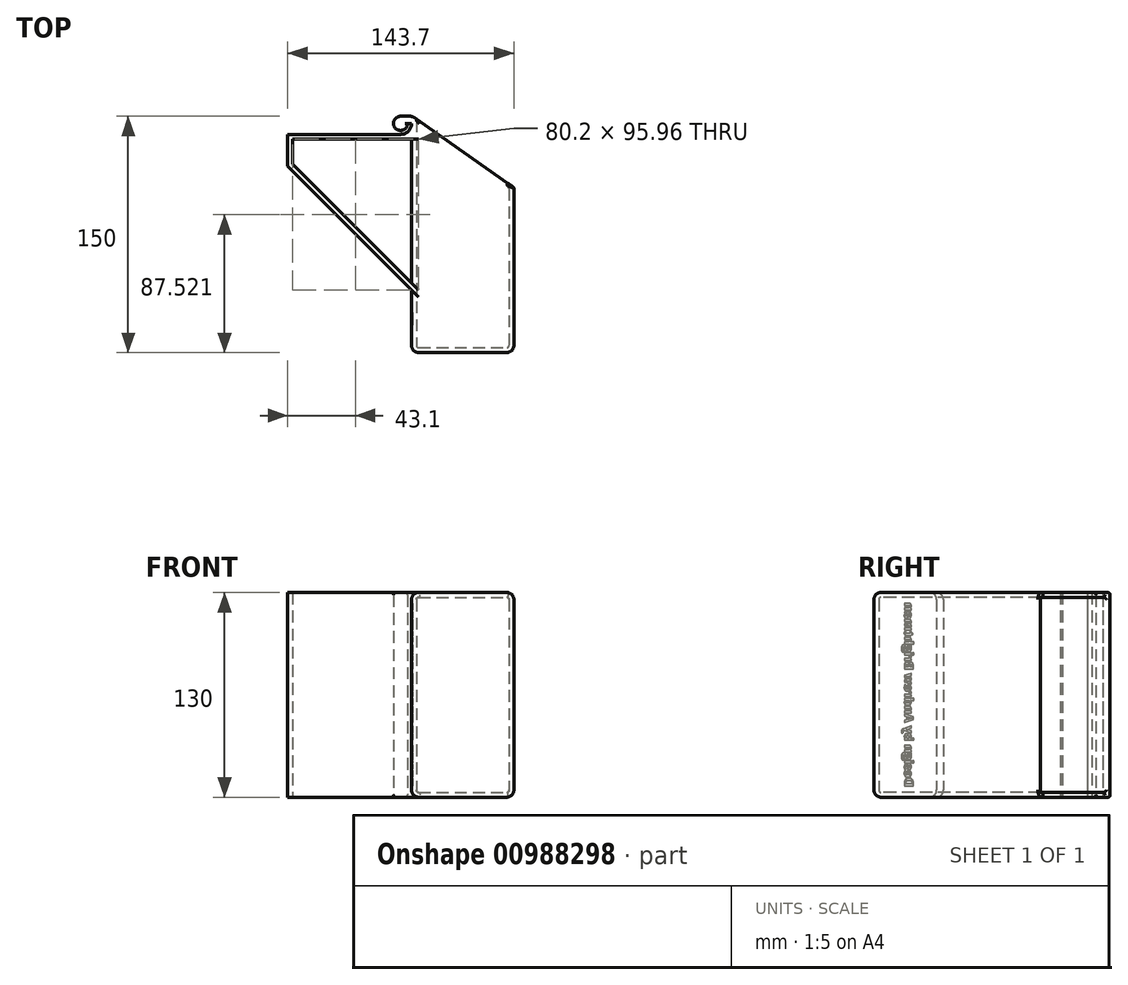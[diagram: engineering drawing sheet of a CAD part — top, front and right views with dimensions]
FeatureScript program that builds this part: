
annotation { "Feature Type Name" : "Feature", "Feature Type Description" : "" }
export const myFeature = defineFeature(function(context is Context, id is Id, definition is map)
    precondition{}
    {
        {
            assignVariable(context, id + "F0", {"variableType" : VariableType.LENGTH, "name" : "wallThickness", "lengthValue" : 3 * mm});
        }
        {
            var Q0;
            Q0=qCreatedBy(makeId("Top.planeOp"),FACE);
            var sketch = newSketch(context, id + "F1", { "sketchPlane" : qUnion([Q0])});
            skLineSegment(sketch, "E0", {"start": v(0, 0) * mm, "end": v(71.7, 0) * mm, "construction": true});
            skLineSegment(sketch, "E1", {"start": v(78.7, 7) * mm, "end": v(78.7, 7) * mm});
            skPoint(sketch, "E2.visualSharp", {"position": v(78.7, 0) * mm});
            skArc(sketch, "E2.filletArc", {"start": v(71.7, 0) * mm, "mid": v(76.65, 2.05) * mm, "end": v(78.7, 7) * mm, "construction": true});
            skArc(sketch, "E3.0", {"start": v(71.7, 2.5) * mm, "mid": v(74.88, 3.82) * mm, "end": v(76.2, 7) * mm, "construction": true});
            skLineSegment(sketch, "E3.1", {"start": v(0, 2.5) * mm, "end": v(71.7, 2.5) * mm, "construction": true});
            skLineSegment(sketch, "E4", {"start": v(0, 2.5) * mm, "end": v(0, 0) * mm, "construction": true});
            skLineSegment(sketch, "E5", {"start": v(76.2, 7) * mm, "end": v(78.7, 7) * mm, "construction": true});
            skLineSegment(sketch, "E6", {"start": v(0, 0) * mm, "end": v(0, -20) * mm});
            skLineSegment(sketch, "E7", {"start": v(0, -20) * mm, "end": v(0, -20) * mm});
            skLineSegment(sketch, "E8", {"start": v(78.7, -138.5) * mm, "end": v(143.7, -138.5) * mm});
            skLineSegment(sketch, "E9", {"start": v(143.7, -138.5) * mm, "end": v(143.7, -33.63) * mm});
            skLineSegment(sketch, "E10", {"start": v(143.7, -33.63) * mm, "end": v(80.54, 10.6) * mm});
            skArc(sketch, "E11.0", {"start": v(71.7, 0) * mm, "mid": v(76.65, 2.05) * mm, "end": v(78.7, 7) * mm});
            skLineSegment(sketch, "E11.1", {"start": v(0, 0) * mm, "end": v(71.7, 0) * mm});
            skArc(sketch, "E12", {"start": v(71.7, 11.5) * mm, "mid": v(68.52, 3.82) * mm, "end": v(76.2, 7) * mm});
            skLineSegment(sketch, "E13", {"start": v(77.67, 11.5) * mm, "end": v(71.7, 11.5) * mm});
            skLineSegment(sketch, "E14", {"start": v(76.2, 7) * mm, "end": v(78.7, 7) * mm});
            skLineSegment(sketch, "E15", {"start": v(78.7, 7) * mm, "end": v(81, 10.28) * mm, "construction": true});
            skPoint(sketch, "E16.visualSharp", {"position": v(79.25, 11.5) * mm});
            skArc(sketch, "E16.filletArc", {"start": v(80.54, 10.6) * mm, "mid": v(79.17, 11.27) * mm, "end": v(77.67, 11.5) * mm});
            skLineSegment(sketch, "E17", {"start": v(0, -20) * mm, "end": v(78.7, -98.7) * mm});
            skLineSegment(sketch, "E18.trimOffspring", {"start": v(78.7, -98.7) * mm, "end": v(78.7, -138.5) * mm});
            skLineSegment(sketch, "E19.0", {"start": v(3, -18.76) * mm, "end": v(78.7, -94.46) * mm});
            skLineSegment(sketch, "E20", {"start": v(78.7, -94.46) * mm, "end": v(78.7, -3) * mm});
            skLineSegment(sketch, "E21", {"start": v(78.7, -3) * mm, "end": v(3, -3) * mm});
            skLineSegment(sketch, "E22", {"start": v(3, -18.76) * mm, "end": v(3, -3) * mm});
            skSolve(sketch);
        }
        {
            var Q0;
            Q0 = qSketchRegion(id + "F1", true);
            extrude(context, id + "F2", {"entities" : qUnion([Q0]), "depth" : 130 * mm, "offsetDistance" : 25 * mm});
        }
        {
            var Q0;
            Q0=makeQuery(id+"F2.opExtrude","SWEPT_FACE",FACE,{"disambiguationData":[OSD([sQuery(id+"F1.wireOp",EDGE,"E8")])]});
            cPlane(context, id + "F3", {"entities" : qUnion([Q0]), "cplaneType" : CPlaneType.OFFSET, "offset" : getVariable(context, 'wallThickness'), "oppositeDirection" : true, "width" : 150 * mm, "height" : 150 * mm});
        }
        {
            var Q0;
            Q0=qCreatedBy(id+"F3.planeOp",FACE);
            var sketch = newSketch(context, id + "F4", { "sketchPlane" : qUnion([Q0])});
            skLineSegment(sketch, "E23.0", {"start": v(81.7, 127) * mm, "end": v(81.7, 3) * mm});
            skLineSegment(sketch, "E23.1", {"start": v(81.7, 127) * mm, "end": v(140.7, 127) * mm});
            skLineSegment(sketch, "E23.2", {"start": v(140.7, 127) * mm, "end": v(140.7, 3) * mm});
            skLineSegment(sketch, "E23.3", {"start": v(81.7, 3) * mm, "end": v(140.7, 3) * mm});
            skSolve(sketch);
        }
        {
            var Q0;
            Q0 = qSketchRegion(id + "F4", true);
            extrude(context, id + "F5", {"entities" : qUnion([Q0]), "operationType" : NewBodyOperationType.REMOVE, "endBound" : BoundingType.THROUGH_ALL, "oppositeDirection" : true, "depth" : 25 * mm, "offsetDistance" : 25 * mm});
        }
        {
            var Q0;
            Q0=makeQuery(id+"F5.boolean.opBoolean","COPY",FACE,{"derivedFrom":makeQuery(id+"F5.opExtrude","CAP_FACE",FACE,{"disambiguationData":[OSD([sQuery(id+"F4.wireOp",EDGE,"E23.0"),sQuery(id+"F4.wireOp",EDGE,"E23.1"),sQuery(id+"F4.wireOp",EDGE,"E23.2"),sQuery(id+"F4.wireOp",EDGE,"E23.3")])],"isStart":true})});
            var Q1;
            Q1=makeQuery(id+"F5.boolean.opBoolean","COPY",EDGE,{"derivedFrom":makeQuery(id+"F5.opExtrude","SWEPT_EDGE",EDGE,{"disambiguationData":[OSD([sQuery(id+"F4.wireOp",EDGE,"E23.0"),sQuery(id+"F4.wireOp",EDGE,"E23.3")])]})});
            var Q2;
            Q2=makeQuery(id+"F5.boolean.opBoolean","COPY",EDGE,{"derivedFrom":makeQuery(id+"F5.opExtrude","SWEPT_EDGE",EDGE,{"disambiguationData":[OSD([sQuery(id+"F4.wireOp",EDGE,"E23.2"),sQuery(id+"F4.wireOp",EDGE,"E23.3")])]})});
            var Q3;
            Q3=makeQuery(id+"F5.boolean.opBoolean","COPY",EDGE,{"derivedFrom":makeQuery(id+"F5.opExtrude","SWEPT_EDGE",EDGE,{"disambiguationData":[OSD([sQuery(id+"F4.wireOp",EDGE,"E23.0"),sQuery(id+"F4.wireOp",EDGE,"E23.1")])]})});
            var Q4;
            Q4=makeQuery(id+"F5.boolean.opBoolean","COPY",EDGE,{"derivedFrom":makeQuery(id+"F5.opExtrude","SWEPT_EDGE",EDGE,{"disambiguationData":[OSD([sQuery(id+"F4.wireOp",EDGE,"E23.1"),sQuery(id+"F4.wireOp",EDGE,"E23.2")])]})});
            fillet(context, id + "F6", {"entities" : qUnion([Q0, Q1, Q2, Q3, Q4]), "radius" : getVariable(context, 'wallThickness') / 2, "tangentPropagation" : true, "defaultsChanged" : true, "vertexSettings" : [], "allowEdgeOverflow" : false});
        }
        {
            var Q0;
            Q0=makeQuery(id+"F2.opExtrude","CAP_EDGE",EDGE,{"disambiguationData":[OSD([sQuery(id+"F1.wireOp",EDGE,"E9")])],"isStart":false});
            var Q1;
            Q1=makeQuery(id+"F2.opExtrude","CAP_EDGE",EDGE,{"disambiguationData":[OSD([sQuery(id+"F1.wireOp",EDGE,"E9")])],"isStart":true});
            var Q2;
            Q2=makeQuery(id+"F2.opExtrude","CAP_EDGE",EDGE,{"disambiguationData":[OSD([sQuery(id+"F1.wireOp",EDGE,"E20")])],"isStart":false});
            var Q3;
            Q3=makeQuery(id+"F2.opExtrude","CAP_EDGE",EDGE,{"disambiguationData":[OSD([sQuery(id+"F1.wireOp",EDGE,"E18.trimOffspring")])],"isStart":false});
            var Q4;
            Q4=makeQuery(id+"F2.opExtrude","CAP_EDGE",EDGE,{"disambiguationData":[OSD([sQuery(id+"F1.wireOp",EDGE,"E18.trimOffspring")])],"isStart":true});
            var Q5;
            Q5=makeQuery(id+"F2.opExtrude","CAP_EDGE",EDGE,{"disambiguationData":[OSD([sQuery(id+"F1.wireOp",EDGE,"E20")])],"isStart":true});
            var Q6;
            Q6=makeQuery(id+"F2.opExtrude","SWEPT_FACE",FACE,{"disambiguationData":[OSD([sQuery(id+"F1.wireOp",EDGE,"E8")])]});
            fillet(context, id + "F7", {"entities" : qUnion([Q0, Q1, Q2, Q3, Q4, Q5, Q6]), "tangentPropagation" : true, "radius" : getVariable(context, 'wallThickness') + getVariable(context, 'wallThickness') / 2, "defaultsChanged" : false, "vertexSettings" : [], "allowEdgeOverflow" : false});
        }
        {
            var Q0;
            Q0=makeQuery(id+"F2.opExtrude","SWEPT_FACE",FACE,{"disambiguationData":[OSD([sQuery(id+"F1.wireOp",EDGE,"E10")])]});
            fillet(context, id + "F8", {"entities" : qUnion([Q0]), "tangentPropagation" : true, "radius" : getVariable(context, 'wallThickness') / 2, "defaultsChanged" : false, "vertexSettings" : [], "allowEdgeOverflow" : false});
        }
        {
            var Q0;
            Q0=makeQuery(id+"F2.opExtrude","SWEPT_FACE",FACE,{"disambiguationData":[OSD([sQuery(id+"F1.wireOp",EDGE,"E18.trimOffspring")])]});
            var sketch = newSketch(context, id + "F9", { "sketchPlane" : qUnion([Q0])});
            skText(sketch, "E24", { "text": "Design by Andrew Brightman", "fontName": "OpenSans-Bold.ttf"});
            skLineSegment(sketch, "E25", {"start": v(113.45, 14.8) * mm, "end": v(98.7, 14.8) * mm, "construction": true});
            skLineSegment(sketch, "E26", {"start": v(119.25, 12.33) * mm, "end": v(134, 12.33) * mm, "construction": true});
            const initialGuessF9  = {"E24": [0.11925, 0.0065, 0, 1, 0.0058]};
            skSetInitialGuess(sketch, initialGuessF9);
            skSolve(sketch);
        }
        {
            var Q0;
            Q0 = qSketchRegion(id + "F9", true);
            extrude(context, id + "F10", {"entities" : qUnion([Q0]), "operationType" : NewBodyOperationType.REMOVE, "oppositeDirection" : true, "depth" : 0.5 * mm, "offsetDistance" : 25 * mm});
        }
    });
